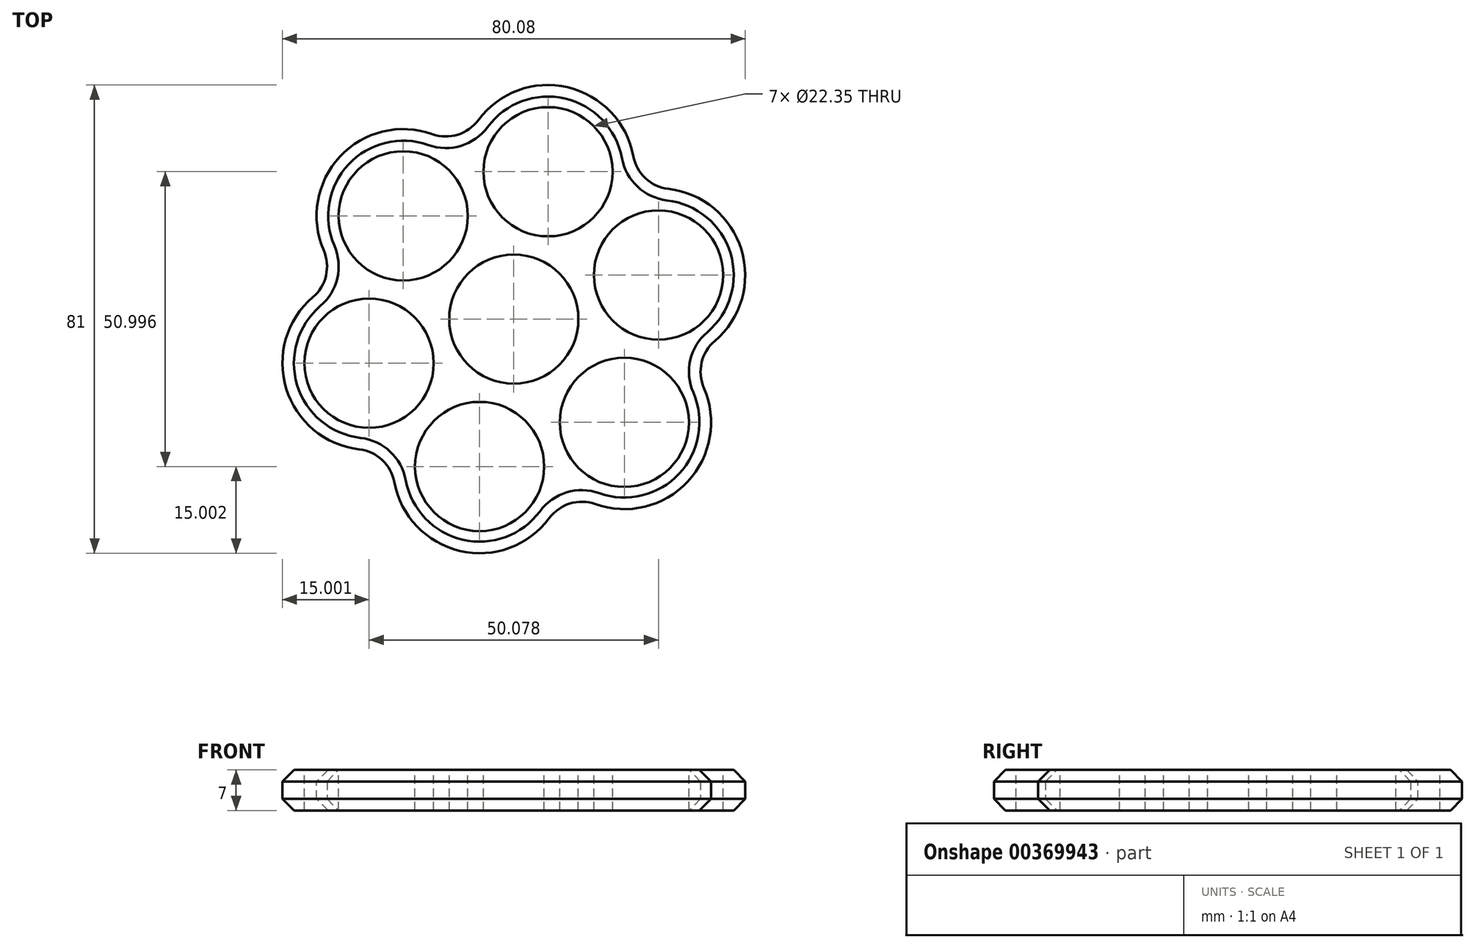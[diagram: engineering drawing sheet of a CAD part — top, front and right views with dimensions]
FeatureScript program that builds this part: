
annotation { "Feature Type Name" : "Feature", "Feature Type Description" : "" }
export const myFeature = defineFeature(function(context is Context, id is Id, definition is map)
    precondition{}
    {
        {
            var Q0;
            Q0=qCreatedBy(makeId("Top.planeOp"),FACE);
            var sketch = newSketch(context, id + "F0", { "sketchPlane" : qUnion([Q0])});
            skCircle(sketch, "E0", {"center": v(0, 0) * mm, "radius": 11.18 * mm});
            skLineSegment(sketch, "E1", {"start": v(0, 0) * mm, "end": v(-19.13, 17.87) * mm});
            skLineSegment(sketch, "E2", {"start": v(0, 0) * mm, "end": v(25.04, 7.63) * mm});
            skLineSegment(sketch, "E3", {"start": v(0, 0) * mm, "end": v(-5.91, -25.5) * mm});
            skCircle(sketch, "E4", {"center": v(-19.13, 17.87) * mm, "radius": 11.18 * mm});
            skCircle(sketch, "E5", {"center": v(25.04, 7.63) * mm, "radius": 11.18 * mm});
            skCircle(sketch, "E6", {"center": v(-5.91, -25.5) * mm, "radius": 11.18 * mm});
            skCircle(sketch, "E7", {"center": v(0, 0) * mm, "radius": 15 * mm});
            skCircle(sketch, "E8", {"center": v(-19.13, 17.87) * mm, "radius": 15 * mm});
            skCircle(sketch, "E9", {"center": v(25.04, 7.63) * mm, "radius": 15 * mm});
            skCircle(sketch, "E10", {"center": v(-5.91, -25.5) * mm, "radius": 15 * mm});
            skLineSegment(sketch, "E11", {"start": v(-19.13, 17.87) * mm, "end": v(-8.88, 28.83) * mm});
            skLineSegment(sketch, "E12", {"start": v(25.04, 7.63) * mm, "end": v(20.67, 21.98) * mm});
            skLineSegment(sketch, "E13", {"start": v(-5.91, -25.5) * mm, "end": v(8.7, -28.89) * mm});
            skLineSegment(sketch, "E14", {"start": v(-5.91, -25.5) * mm, "end": v(-20.53, -22.1) * mm});
            skLineSegment(sketch, "E15", {"start": v(-19.13, 17.87) * mm, "end": v(-29.37, 6.91) * mm});
            skLineSegment(sketch, "E16", {"start": v(25.04, 7.63) * mm, "end": v(29.41, -6.72) * mm});
            skLineSegment(sketch, "E17", {"start": v(0, 0) * mm, "end": v(5.91, 25.5) * mm});
            skLineSegment(sketch, "E18", {"start": v(0, 0) * mm, "end": v(19.13, -17.87) * mm});
            skLineSegment(sketch, "E19", {"start": v(0, 0) * mm, "end": v(-25.04, -7.63) * mm});
            skCircle(sketch, "E20", {"center": v(-25.04, -7.63) * mm, "radius": 11.18 * mm});
            skCircle(sketch, "E21", {"center": v(5.91, 25.5) * mm, "radius": 11.18 * mm});
            skCircle(sketch, "E22", {"center": v(19.13, -17.87) * mm, "radius": 11.18 * mm});
            skCircle(sketch, "E23", {"center": v(-25.04, -7.63) * mm, "radius": 15 * mm});
            skCircle(sketch, "E24", {"center": v(5.91, 25.5) * mm, "radius": 15 * mm});
            skCircle(sketch, "E25", {"center": v(19.13, -17.87) * mm, "radius": 15 * mm});
            skSolve(sketch);
        }
        {
            var Q0;
            {var subQ0=sQuery(id+"F0.wireOp",EDGE,"E11");var subQ1=sQuery(id+"F0.wireOp",EDGE,"E4");var subQ2=makeQuery(id+"F0.imprint","INTERSECT",VERTEX,{"derivedFrom":[subQ1,subQ0]});Q0=makeQuery(id+"F0.imprint","IMPRINT",FACE,{"disambiguationData":[TD([[makeQuery(id+"F0.imprint","IMPRINT",EDGE,{"disambiguationData":[TD([[subQ2,1.0]])],"derivedFrom":subQ1}),-1.0]])]});}
            var Q1;
            {var subQ0=sQuery(id+"F0.wireOp",EDGE,"E11");var subQ1=sQuery(id+"F0.wireOp",EDGE,"E4");var subQ2=makeQuery(id+"F0.imprint","INTERSECT",VERTEX,{"derivedFrom":[subQ1,subQ0]});Q1=makeQuery(id+"F0.imprint","IMPRINT",FACE,{"disambiguationData":[TD([[makeQuery(id+"F0.imprint","IMPRINT",EDGE,{"disambiguationData":[TD([[subQ2,-1.0]])],"derivedFrom":subQ1}),-1.0]])]});}
            var Q2;
            {var subQ0=sQuery(id+"F0.wireOp",EDGE,"E15");var subQ1=sQuery(id+"F0.wireOp",EDGE,"E4");var subQ2=makeQuery(id+"F0.imprint","INTERSECT",VERTEX,{"derivedFrom":[subQ1,subQ0]});Q2=makeQuery(id+"F0.imprint","IMPRINT",FACE,{"disambiguationData":[TD([[makeQuery(id+"F0.imprint","IMPRINT",EDGE,{"disambiguationData":[TD([[subQ2,-1.0]])],"derivedFrom":subQ1}),-1.0]])]});}
            var Q3;
            {var subQ0=sQuery(id+"F0.wireOp",EDGE,"E24");var subQ1=sQuery(id+"F0.wireOp",EDGE,"E5");var subQ2=makeQuery(id+"F0.imprint","INTERSECT",VERTEX,{"derivedFrom":[subQ1,subQ0]});Q3=makeQuery(id+"F0.imprint","IMPRINT",FACE,{"disambiguationData":[TD([[makeQuery(id+"F0.imprint","IMPRINT",EDGE,{"disambiguationData":[TD([[subQ2,1.0]])],"derivedFrom":subQ1}),-1.0]])]});}
            var Q4;
            {var subQ0=sQuery(id+"F0.wireOp",EDGE,"E25");var subQ1=sQuery(id+"F0.wireOp",EDGE,"E5");var subQ2=makeQuery(id+"F0.imprint","INTERSECT",VERTEX,{"derivedFrom":[subQ1,subQ0]});Q4=makeQuery(id+"F0.imprint","IMPRINT",FACE,{"disambiguationData":[TD([[makeQuery(id+"F0.imprint","IMPRINT",EDGE,{"disambiguationData":[TD([[subQ2,-1.0]])],"derivedFrom":subQ1}),-1.0]])]});}
            var Q5;
            {var subQ0=sQuery(id+"F0.wireOp",EDGE,"E12");var subQ1=sQuery(id+"F0.wireOp",EDGE,"E5");var subQ2=makeQuery(id+"F0.imprint","INTERSECT",VERTEX,{"derivedFrom":[subQ1,subQ0]});Q5=makeQuery(id+"F0.imprint","IMPRINT",FACE,{"disambiguationData":[TD([[makeQuery(id+"F0.imprint","IMPRINT",EDGE,{"disambiguationData":[TD([[subQ2,1.0]])],"derivedFrom":subQ1}),-1.0]])]});}
            var Q6;
            {var subQ0=sQuery(id+"F0.wireOp",EDGE,"E23");var subQ1=sQuery(id+"F0.wireOp",EDGE,"E6");var subQ2=makeQuery(id+"F0.imprint","INTERSECT",VERTEX,{"derivedFrom":[subQ1,subQ0]});Q6=makeQuery(id+"F0.imprint","IMPRINT",FACE,{"disambiguationData":[TD([[makeQuery(id+"F0.imprint","IMPRINT",EDGE,{"disambiguationData":[TD([[subQ2,-1.0]])],"derivedFrom":subQ1}),-1.0]])]});}
            var Q7;
            {var subQ0=sQuery(id+"F0.wireOp",EDGE,"E14");var subQ1=sQuery(id+"F0.wireOp",EDGE,"E6");var subQ2=makeQuery(id+"F0.imprint","INTERSECT",VERTEX,{"derivedFrom":[subQ1,subQ0]});Q7=makeQuery(id+"F0.imprint","IMPRINT",FACE,{"disambiguationData":[TD([[makeQuery(id+"F0.imprint","IMPRINT",EDGE,{"disambiguationData":[TD([[subQ2,-1.0]])],"derivedFrom":subQ1}),-1.0]])]});}
            var Q8;
            {var subQ0=sQuery(id+"F0.wireOp",EDGE,"E25");var subQ1=sQuery(id+"F0.wireOp",EDGE,"E6");var subQ2=makeQuery(id+"F0.imprint","INTERSECT",VERTEX,{"derivedFrom":[subQ1,subQ0]});Q8=makeQuery(id+"F0.imprint","IMPRINT",FACE,{"disambiguationData":[TD([[makeQuery(id+"F0.imprint","IMPRINT",EDGE,{"disambiguationData":[TD([[subQ2,1.0]])],"derivedFrom":subQ1}),-1.0]])]});}
            var Q9;
            {var subQ0=sQuery(id+"F0.wireOp",EDGE,"E24");var subQ1=sQuery(id+"F0.wireOp",EDGE,"E8");var subQ2=makeQuery(id+"F0.imprint","INTERSECT",VERTEX,{"disambiguationData":[OD(0.0)],"derivedFrom":[subQ1,subQ0]});Q9=makeQuery(id+"F0.imprint","IMPRINT",FACE,{"disambiguationData":[TD([[makeQuery(id+"F0.imprint","IMPRINT",EDGE,{"disambiguationData":[TD([[subQ2,1.0]])],"derivedFrom":subQ1}),-1.0]])]});}
            var Q10;
            {var subQ0=sQuery(id+"F0.wireOp",EDGE,"E23");var subQ1=sQuery(id+"F0.wireOp",EDGE,"E8");var subQ2=makeQuery(id+"F0.imprint","INTERSECT",VERTEX,{"disambiguationData":[OD(0.0)],"derivedFrom":[subQ1,subQ0]});Q10=makeQuery(id+"F0.imprint","IMPRINT",FACE,{"disambiguationData":[TD([[makeQuery(id+"F0.imprint","IMPRINT",EDGE,{"disambiguationData":[TD([[subQ2,-1.0]])],"derivedFrom":subQ1}),-1.0]])]});}
            var Q11;
            {var subQ0=sQuery(id+"F0.wireOp",EDGE,"E25");var subQ1=sQuery(id+"F0.wireOp",EDGE,"E9");var subQ2=makeQuery(id+"F0.imprint","INTERSECT",VERTEX,{"disambiguationData":[OD(0.0)],"derivedFrom":[subQ1,subQ0]});Q11=makeQuery(id+"F0.imprint","IMPRINT",FACE,{"disambiguationData":[TD([[makeQuery(id+"F0.imprint","IMPRINT",EDGE,{"disambiguationData":[TD([[subQ2,1.0]])],"derivedFrom":subQ1}),-1.0]])]});}
            var Q12;
            {var subQ0=sQuery(id+"F0.wireOp",EDGE,"E24");var subQ1=sQuery(id+"F0.wireOp",EDGE,"E8");var subQ2=makeQuery(id+"F0.imprint","INTERSECT",VERTEX,{"disambiguationData":[OD(0.0)],"derivedFrom":[subQ1,subQ0]});Q12=makeQuery(id+"F0.imprint","IMPRINT",FACE,{"disambiguationData":[TD([[makeQuery(id+"F0.imprint","IMPRINT",EDGE,{"disambiguationData":[TD([[subQ2,1.0]])],"derivedFrom":subQ1}),1.0]])]});}
            var Q13;
            {var subQ0=sQuery(id+"F0.wireOp",EDGE,"E23");var subQ1=sQuery(id+"F0.wireOp",EDGE,"E8");var subQ2=makeQuery(id+"F0.imprint","INTERSECT",VERTEX,{"disambiguationData":[OD(0.0)],"derivedFrom":[subQ1,subQ0]});Q13=makeQuery(id+"F0.imprint","IMPRINT",FACE,{"disambiguationData":[TD([[makeQuery(id+"F0.imprint","IMPRINT",EDGE,{"disambiguationData":[TD([[subQ2,-1.0]])],"derivedFrom":subQ1}),1.0]])]});}
            var Q14;
            {var subQ0=sQuery(id+"F0.wireOp",EDGE,"E24");var subQ1=sQuery(id+"F0.wireOp",EDGE,"E9");var subQ2=makeQuery(id+"F0.imprint","INTERSECT",VERTEX,{"disambiguationData":[OD(0.0)],"derivedFrom":[subQ1,subQ0]});Q14=makeQuery(id+"F0.imprint","IMPRINT",FACE,{"disambiguationData":[TD([[makeQuery(id+"F0.imprint","IMPRINT",EDGE,{"disambiguationData":[TD([[subQ2,-1.0]])],"derivedFrom":subQ1}),1.0]])]});}
            var Q15;
            {var subQ0=sQuery(id+"F0.wireOp",EDGE,"E25");var subQ1=sQuery(id+"F0.wireOp",EDGE,"E9");var subQ2=makeQuery(id+"F0.imprint","INTERSECT",VERTEX,{"disambiguationData":[OD(1.0)],"derivedFrom":[subQ1,subQ0]});Q15=makeQuery(id+"F0.imprint","IMPRINT",FACE,{"disambiguationData":[TD([[makeQuery(id+"F0.imprint","IMPRINT",EDGE,{"disambiguationData":[TD([[subQ2,-1.0]])],"derivedFrom":subQ1}),1.0]])]});}
            var Q16;
            {var subQ0=sQuery(id+"F0.wireOp",EDGE,"E25");var subQ1=sQuery(id+"F0.wireOp",EDGE,"E10");var subQ2=makeQuery(id+"F0.imprint","INTERSECT",VERTEX,{"disambiguationData":[OD(1.0)],"derivedFrom":[subQ1,subQ0]});Q16=makeQuery(id+"F0.imprint","IMPRINT",FACE,{"disambiguationData":[TD([[makeQuery(id+"F0.imprint","IMPRINT",EDGE,{"disambiguationData":[TD([[subQ2,1.0]])],"derivedFrom":subQ1}),1.0]])]});}
            var Q17;
            {var subQ0=sQuery(id+"F0.wireOp",EDGE,"E23");var subQ1=sQuery(id+"F0.wireOp",EDGE,"E10");var subQ2=makeQuery(id+"F0.imprint","INTERSECT",VERTEX,{"disambiguationData":[OD(1.0)],"derivedFrom":[subQ1,subQ0]});Q17=makeQuery(id+"F0.imprint","IMPRINT",FACE,{"disambiguationData":[TD([[makeQuery(id+"F0.imprint","IMPRINT",EDGE,{"disambiguationData":[TD([[subQ2,-1.0]])],"derivedFrom":subQ1}),1.0]])]});}
            var Q18;
            {var subQ3=sQuery(id+"F0.wireOp",EDGE,"E7");var subQ5=sQuery(id+"F0.wireOp",EDGE,"E8");var subQ6=makeQuery(id+"F0.imprint","INTERSECT",VERTEX,{"disambiguationData":[OD(0.0)],"derivedFrom":[subQ3,subQ5]});Q18=makeQuery(id+"F0.imprint","IMPRINT",FACE,{"disambiguationData":[TD([[makeQuery(id+"F0.imprint","IMPRINT",EDGE,{"disambiguationData":[TD([[subQ6,-1.0]])],"derivedFrom":subQ5}),1.0]])]});}
            var Q19;
            {var subQ0=sQuery(id+"F0.wireOp",EDGE,"E8");var subQ3=sQuery(id+"F0.wireOp",EDGE,"E7");var subQ5=makeQuery(id+"F0.imprint","INTERSECT",VERTEX,{"disambiguationData":[OD(1.0)],"derivedFrom":[subQ3,subQ0]});Q19=makeQuery(id+"F0.imprint","IMPRINT",FACE,{"disambiguationData":[TD([[makeQuery(id+"F0.imprint","IMPRINT",EDGE,{"disambiguationData":[TD([[subQ5,1.0]])],"derivedFrom":subQ3}),1.0]])]});}
            var Q20;
            {var subQ3=sQuery(id+"F0.wireOp",EDGE,"E7");var subQ5=sQuery(id+"F0.wireOp",EDGE,"E8");var subQ6=makeQuery(id+"F0.imprint","INTERSECT",VERTEX,{"disambiguationData":[OD(1.0)],"derivedFrom":[subQ3,subQ5]});Q20=makeQuery(id+"F0.imprint","IMPRINT",FACE,{"disambiguationData":[TD([[makeQuery(id+"F0.imprint","IMPRINT",EDGE,{"disambiguationData":[TD([[subQ6,1.0]])],"derivedFrom":subQ5}),1.0]])]});}
            var Q21;
            {var subQ0=sQuery(id+"F0.wireOp",EDGE,"E8");var subQ3=sQuery(id+"F0.wireOp",EDGE,"E7");var subQ5=makeQuery(id+"F0.imprint","INTERSECT",VERTEX,{"disambiguationData":[OD(0.0)],"derivedFrom":[subQ3,subQ0]});Q21=makeQuery(id+"F0.imprint","IMPRINT",FACE,{"disambiguationData":[TD([[makeQuery(id+"F0.imprint","IMPRINT",EDGE,{"disambiguationData":[TD([[subQ5,-1.0]])],"derivedFrom":subQ3}),1.0]])]});}
            var Q22;
            {var subQ3=sQuery(id+"F0.wireOp",EDGE,"E21");var subQ5=sQuery(id+"F0.wireOp",EDGE,"E8");var subQ6=makeQuery(id+"F0.imprint","INTERSECT",VERTEX,{"derivedFrom":[subQ5,subQ3]});Q22=makeQuery(id+"F0.imprint","IMPRINT",FACE,{"disambiguationData":[TD([[makeQuery(id+"F0.imprint","IMPRINT",EDGE,{"disambiguationData":[TD([[subQ6,1.0]])],"derivedFrom":subQ5}),-1.0]])]});}
            var Q23;
            {var subQ0=sQuery(id+"F0.wireOp",EDGE,"E24");var subQ1=sQuery(id+"F0.wireOp",EDGE,"E7");var subQ2=makeQuery(id+"F0.imprint","INTERSECT",VERTEX,{"disambiguationData":[OD(1.0)],"derivedFrom":[subQ1,subQ0]});Q23=makeQuery(id+"F0.imprint","IMPRINT",FACE,{"disambiguationData":[TD([[makeQuery(id+"F0.imprint","IMPRINT",EDGE,{"disambiguationData":[TD([[subQ2,1.0]])],"derivedFrom":subQ1}),1.0]])]});}
            var Q24;
            {var subQ0=sQuery(id+"F0.wireOp",EDGE,"E24");var subQ1=sQuery(id+"F0.wireOp",EDGE,"E7");var subQ2=makeQuery(id+"F0.imprint","INTERSECT",VERTEX,{"disambiguationData":[OD(0.0)],"derivedFrom":[subQ1,subQ0]});Q24=makeQuery(id+"F0.imprint","IMPRINT",FACE,{"disambiguationData":[TD([[makeQuery(id+"F0.imprint","IMPRINT",EDGE,{"disambiguationData":[TD([[subQ2,-1.0]])],"derivedFrom":subQ1}),1.0]])]});}
            var Q25;
            {var subQ3=sQuery(id+"F0.wireOp",EDGE,"E21");var subQ5=sQuery(id+"F0.wireOp",EDGE,"E9");var subQ7=makeQuery(id+"F0.imprint","INTERSECT",VERTEX,{"derivedFrom":[subQ5,subQ3]});Q25=makeQuery(id+"F0.imprint","IMPRINT",FACE,{"disambiguationData":[TD([[makeQuery(id+"F0.imprint","IMPRINT",EDGE,{"disambiguationData":[TD([[subQ7,-1.0]])],"derivedFrom":subQ5}),-1.0]])]});}
            var Q26;
            {var subQ3=sQuery(id+"F0.wireOp",EDGE,"E7");var subQ5=sQuery(id+"F0.wireOp",EDGE,"E9");var subQ6=makeQuery(id+"F0.imprint","INTERSECT",VERTEX,{"disambiguationData":[OD(0.0)],"derivedFrom":[subQ3,subQ5]});Q26=makeQuery(id+"F0.imprint","IMPRINT",FACE,{"disambiguationData":[TD([[makeQuery(id+"F0.imprint","IMPRINT",EDGE,{"disambiguationData":[TD([[subQ6,1.0]])],"derivedFrom":subQ5}),1.0]])]});}
            var Q27;
            {var subQ0=sQuery(id+"F0.wireOp",EDGE,"E9");var subQ3=sQuery(id+"F0.wireOp",EDGE,"E7");var subQ5=makeQuery(id+"F0.imprint","INTERSECT",VERTEX,{"disambiguationData":[OD(0.0)],"derivedFrom":[subQ3,subQ0]});Q27=makeQuery(id+"F0.imprint","IMPRINT",FACE,{"disambiguationData":[TD([[makeQuery(id+"F0.imprint","IMPRINT",EDGE,{"disambiguationData":[TD([[subQ5,1.0]])],"derivedFrom":subQ3}),1.0]])]});}
            var Q28;
            {var subQ0=sQuery(id+"F0.wireOp",EDGE,"E9");var subQ3=sQuery(id+"F0.wireOp",EDGE,"E7");var subQ5=makeQuery(id+"F0.imprint","INTERSECT",VERTEX,{"disambiguationData":[OD(1.0)],"derivedFrom":[subQ3,subQ0]});Q28=makeQuery(id+"F0.imprint","IMPRINT",FACE,{"disambiguationData":[TD([[makeQuery(id+"F0.imprint","IMPRINT",EDGE,{"disambiguationData":[TD([[subQ5,-1.0]])],"derivedFrom":subQ3}),1.0]])]});}
            var Q29;
            {var subQ3=sQuery(id+"F0.wireOp",EDGE,"E7");var subQ5=sQuery(id+"F0.wireOp",EDGE,"E9");var subQ6=makeQuery(id+"F0.imprint","INTERSECT",VERTEX,{"disambiguationData":[OD(1.0)],"derivedFrom":[subQ3,subQ5]});Q29=makeQuery(id+"F0.imprint","IMPRINT",FACE,{"disambiguationData":[TD([[makeQuery(id+"F0.imprint","IMPRINT",EDGE,{"disambiguationData":[TD([[subQ6,-1.0]])],"derivedFrom":subQ5}),1.0]])]});}
            var Q30;
            {var subQ0=sQuery(id+"F0.wireOp",EDGE,"E8");var subQ5=sQuery(id+"F0.wireOp",EDGE,"E7");var subQ6=makeQuery(id+"F0.imprint","INTERSECT",VERTEX,{"disambiguationData":[OD(1.0)],"derivedFrom":[subQ5,subQ0]});Q30=makeQuery(id+"F0.imprint","IMPRINT",FACE,{"disambiguationData":[TD([[makeQuery(id+"F0.imprint","IMPRINT",EDGE,{"disambiguationData":[TD([[subQ6,-1.0]])],"derivedFrom":subQ5}),1.0]])]});}
            var Q31;
            {var subQ3=sQuery(id+"F0.wireOp",EDGE,"E20");var subQ5=sQuery(id+"F0.wireOp",EDGE,"E8");var subQ6=makeQuery(id+"F0.imprint","INTERSECT",VERTEX,{"derivedFrom":[subQ5,subQ3]});Q31=makeQuery(id+"F0.imprint","IMPRINT",FACE,{"disambiguationData":[TD([[makeQuery(id+"F0.imprint","IMPRINT",EDGE,{"disambiguationData":[TD([[subQ6,-1.0]])],"derivedFrom":subQ5}),-1.0]])]});}
            var Q32;
            {var subQ0=sQuery(id+"F0.wireOp",EDGE,"E23");var subQ1=sQuery(id+"F0.wireOp",EDGE,"E7");var subQ2=makeQuery(id+"F0.imprint","INTERSECT",VERTEX,{"disambiguationData":[OD(0.0)],"derivedFrom":[subQ1,subQ0]});Q32=makeQuery(id+"F0.imprint","IMPRINT",FACE,{"disambiguationData":[TD([[makeQuery(id+"F0.imprint","IMPRINT",EDGE,{"disambiguationData":[TD([[subQ2,-1.0]])],"derivedFrom":subQ1}),1.0]])]});}
            var Q33;
            {var subQ0=sQuery(id+"F0.wireOp",EDGE,"E23");var subQ1=sQuery(id+"F0.wireOp",EDGE,"E7");var subQ2=makeQuery(id+"F0.imprint","INTERSECT",VERTEX,{"disambiguationData":[OD(1.0)],"derivedFrom":[subQ1,subQ0]});Q33=makeQuery(id+"F0.imprint","IMPRINT",FACE,{"disambiguationData":[TD([[makeQuery(id+"F0.imprint","IMPRINT",EDGE,{"disambiguationData":[TD([[subQ2,1.0]])],"derivedFrom":subQ1}),1.0]])]});}
            var Q34;
            {var subQ0=sQuery(id+"F0.wireOp",EDGE,"E23");var subQ5=sQuery(id+"F0.wireOp",EDGE,"E10");var subQ6=makeQuery(id+"F0.imprint","INTERSECT",VERTEX,{"disambiguationData":[OD(1.0)],"derivedFrom":[subQ5,subQ0]});Q34=makeQuery(id+"F0.imprint","IMPRINT",FACE,{"disambiguationData":[TD([[makeQuery(id+"F0.imprint","IMPRINT",EDGE,{"disambiguationData":[TD([[subQ6,-1.0]])],"derivedFrom":subQ5}),-1.0]])]});}
            var Q35;
            {var subQ0=sQuery(id+"F0.wireOp",EDGE,"E23");var subQ5=sQuery(id+"F0.wireOp",EDGE,"E7");var subQ7=makeQuery(id+"F0.imprint","INTERSECT",VERTEX,{"disambiguationData":[OD(1.0)],"derivedFrom":[subQ5,subQ0]});Q35=makeQuery(id+"F0.imprint","IMPRINT",FACE,{"disambiguationData":[TD([[makeQuery(id+"F0.imprint","IMPRINT",EDGE,{"disambiguationData":[TD([[subQ7,-1.0]])],"derivedFrom":subQ5}),1.0]])]});}
            var Q36;
            {var subQ0=sQuery(id+"F0.wireOp",EDGE,"E10");var subQ3=sQuery(id+"F0.wireOp",EDGE,"E7");var subQ5=makeQuery(id+"F0.imprint","INTERSECT",VERTEX,{"disambiguationData":[OD(0.0)],"derivedFrom":[subQ3,subQ0]});Q36=makeQuery(id+"F0.imprint","IMPRINT",FACE,{"disambiguationData":[TD([[makeQuery(id+"F0.imprint","IMPRINT",EDGE,{"disambiguationData":[TD([[subQ5,-1.0]])],"derivedFrom":subQ3}),1.0]])]});}
            var Q37;
            {var subQ3=sQuery(id+"F0.wireOp",EDGE,"E7");var subQ5=sQuery(id+"F0.wireOp",EDGE,"E10");var subQ6=makeQuery(id+"F0.imprint","INTERSECT",VERTEX,{"disambiguationData":[OD(0.0)],"derivedFrom":[subQ3,subQ5]});Q37=makeQuery(id+"F0.imprint","IMPRINT",FACE,{"disambiguationData":[TD([[makeQuery(id+"F0.imprint","IMPRINT",EDGE,{"disambiguationData":[TD([[subQ6,-1.0]])],"derivedFrom":subQ5}),1.0]])]});}
            var Q38;
            {var subQ0=sQuery(id+"F0.wireOp",EDGE,"E10");var subQ3=sQuery(id+"F0.wireOp",EDGE,"E7");var subQ5=makeQuery(id+"F0.imprint","INTERSECT",VERTEX,{"disambiguationData":[OD(1.0)],"derivedFrom":[subQ3,subQ0]});Q38=makeQuery(id+"F0.imprint","IMPRINT",FACE,{"disambiguationData":[TD([[makeQuery(id+"F0.imprint","IMPRINT",EDGE,{"disambiguationData":[TD([[subQ5,1.0]])],"derivedFrom":subQ3}),1.0]])]});}
            var Q39;
            {var subQ3=sQuery(id+"F0.wireOp",EDGE,"E7");var subQ5=sQuery(id+"F0.wireOp",EDGE,"E10");var subQ6=makeQuery(id+"F0.imprint","INTERSECT",VERTEX,{"disambiguationData":[OD(1.0)],"derivedFrom":[subQ3,subQ5]});Q39=makeQuery(id+"F0.imprint","IMPRINT",FACE,{"disambiguationData":[TD([[makeQuery(id+"F0.imprint","IMPRINT",EDGE,{"disambiguationData":[TD([[subQ6,1.0]])],"derivedFrom":subQ5}),1.0]])]});}
            var Q40;
            {var subQ0=sQuery(id+"F0.wireOp",EDGE,"E10");var subQ5=sQuery(id+"F0.wireOp",EDGE,"E7");var subQ6=makeQuery(id+"F0.imprint","INTERSECT",VERTEX,{"disambiguationData":[OD(1.0)],"derivedFrom":[subQ5,subQ0]});Q40=makeQuery(id+"F0.imprint","IMPRINT",FACE,{"disambiguationData":[TD([[makeQuery(id+"F0.imprint","IMPRINT",EDGE,{"disambiguationData":[TD([[subQ6,-1.0]])],"derivedFrom":subQ5}),1.0]])]});}
            var Q41;
            {var subQ3=sQuery(id+"F0.wireOp",EDGE,"E25");var subQ5=sQuery(id+"F0.wireOp",EDGE,"E7");var subQ6=makeQuery(id+"F0.imprint","INTERSECT",VERTEX,{"disambiguationData":[OD(1.0)],"derivedFrom":[subQ5,subQ3]});Q41=makeQuery(id+"F0.imprint","IMPRINT",FACE,{"disambiguationData":[TD([[makeQuery(id+"F0.imprint","IMPRINT",EDGE,{"disambiguationData":[TD([[subQ6,-1.0]])],"derivedFrom":subQ5}),1.0]])]});}
            var Q42;
            {var subQ0=sQuery(id+"F0.wireOp",EDGE,"E25");var subQ5=sQuery(id+"F0.wireOp",EDGE,"E9");var subQ7=makeQuery(id+"F0.imprint","INTERSECT",VERTEX,{"disambiguationData":[OD(1.0)],"derivedFrom":[subQ5,subQ0]});Q42=makeQuery(id+"F0.imprint","IMPRINT",FACE,{"disambiguationData":[TD([[makeQuery(id+"F0.imprint","IMPRINT",EDGE,{"disambiguationData":[TD([[subQ7,-1.0]])],"derivedFrom":subQ5}),-1.0]])]});}
            var Q43;
            {var subQ0=sQuery(id+"F0.wireOp",EDGE,"E25");var subQ1=sQuery(id+"F0.wireOp",EDGE,"E7");var subQ2=makeQuery(id+"F0.imprint","INTERSECT",VERTEX,{"disambiguationData":[OD(1.0)],"derivedFrom":[subQ1,subQ0]});Q43=makeQuery(id+"F0.imprint","IMPRINT",FACE,{"disambiguationData":[TD([[makeQuery(id+"F0.imprint","IMPRINT",EDGE,{"disambiguationData":[TD([[subQ2,1.0]])],"derivedFrom":subQ1}),1.0]])]});}
            var Q44;
            {var subQ0=sQuery(id+"F0.wireOp",EDGE,"E25");var subQ1=sQuery(id+"F0.wireOp",EDGE,"E7");var subQ2=makeQuery(id+"F0.imprint","INTERSECT",VERTEX,{"disambiguationData":[OD(0.0)],"derivedFrom":[subQ1,subQ0]});Q44=makeQuery(id+"F0.imprint","IMPRINT",FACE,{"disambiguationData":[TD([[makeQuery(id+"F0.imprint","IMPRINT",EDGE,{"disambiguationData":[TD([[subQ2,-1.0]])],"derivedFrom":subQ1}),1.0]])]});}
            var Q45;
            {var subQ0=sQuery(id+"F0.wireOp",EDGE,"E25");var subQ5=sQuery(id+"F0.wireOp",EDGE,"E10");var subQ6=makeQuery(id+"F0.imprint","INTERSECT",VERTEX,{"disambiguationData":[OD(1.0)],"derivedFrom":[subQ5,subQ0]});Q45=makeQuery(id+"F0.imprint","IMPRINT",FACE,{"disambiguationData":[TD([[makeQuery(id+"F0.imprint","IMPRINT",EDGE,{"disambiguationData":[TD([[subQ6,1.0]])],"derivedFrom":subQ5}),-1.0]])]});}
            var Q46;
            {var subQ0=sQuery(id+"F0.wireOp",EDGE,"E24");var subQ5=sQuery(id+"F0.wireOp",EDGE,"E7");var subQ7=makeQuery(id+"F0.imprint","INTERSECT",VERTEX,{"disambiguationData":[OD(1.0)],"derivedFrom":[subQ5,subQ0]});Q46=makeQuery(id+"F0.imprint","IMPRINT",FACE,{"disambiguationData":[TD([[makeQuery(id+"F0.imprint","IMPRINT",EDGE,{"disambiguationData":[TD([[subQ7,-1.0]])],"derivedFrom":subQ5}),1.0]])]});}
            var Q47;
            {var subQ3=sQuery(id+"F0.wireOp",EDGE,"E9");var subQ5=sQuery(id+"F0.wireOp",EDGE,"E7");var subQ6=makeQuery(id+"F0.imprint","INTERSECT",VERTEX,{"disambiguationData":[OD(0.0)],"derivedFrom":[subQ5,subQ3]});Q47=makeQuery(id+"F0.imprint","IMPRINT",FACE,{"disambiguationData":[TD([[makeQuery(id+"F0.imprint","IMPRINT",EDGE,{"disambiguationData":[TD([[subQ6,-1.0]])],"derivedFrom":subQ5}),1.0]])]});}
            var Q48;
            {var subQ0=sQuery(id+"F0.wireOp",EDGE,"E10");var subQ1=sQuery(id+"F0.wireOp",EDGE,"E7");var subQ2=makeQuery(id+"F0.imprint","INTERSECT",VERTEX,{"disambiguationData":[OD(1.0)],"derivedFrom":[subQ1,subQ0]});Q48=makeQuery(id+"F0.imprint","IMPRINT",FACE,{"disambiguationData":[TD([[makeQuery(id+"F0.imprint","IMPRINT",EDGE,{"disambiguationData":[TD([[subQ2,-1.0]])],"derivedFrom":subQ1}),-1.0]])]});}
            var Q49;
            {var subQ0=sQuery(id+"F0.wireOp",EDGE,"E23");var subQ1=sQuery(id+"F0.wireOp",EDGE,"E7");var subQ2=makeQuery(id+"F0.imprint","INTERSECT",VERTEX,{"disambiguationData":[OD(1.0)],"derivedFrom":[subQ1,subQ0]});Q49=makeQuery(id+"F0.imprint","IMPRINT",FACE,{"disambiguationData":[TD([[makeQuery(id+"F0.imprint","IMPRINT",EDGE,{"disambiguationData":[TD([[subQ2,-1.0]])],"derivedFrom":subQ1}),-1.0]])]});}
            var Q50;
            {var subQ0=sQuery(id+"F0.wireOp",EDGE,"E8");var subQ1=sQuery(id+"F0.wireOp",EDGE,"E7");var subQ2=makeQuery(id+"F0.imprint","INTERSECT",VERTEX,{"disambiguationData":[OD(1.0)],"derivedFrom":[subQ1,subQ0]});Q50=makeQuery(id+"F0.imprint","IMPRINT",FACE,{"disambiguationData":[TD([[makeQuery(id+"F0.imprint","IMPRINT",EDGE,{"disambiguationData":[TD([[subQ2,-1.0]])],"derivedFrom":subQ1}),-1.0]])]});}
            var Q51;
            {var subQ0=sQuery(id+"F0.wireOp",EDGE,"E24");var subQ1=sQuery(id+"F0.wireOp",EDGE,"E7");var subQ2=makeQuery(id+"F0.imprint","INTERSECT",VERTEX,{"disambiguationData":[OD(1.0)],"derivedFrom":[subQ1,subQ0]});Q51=makeQuery(id+"F0.imprint","IMPRINT",FACE,{"disambiguationData":[TD([[makeQuery(id+"F0.imprint","IMPRINT",EDGE,{"disambiguationData":[TD([[subQ2,-1.0]])],"derivedFrom":subQ1}),-1.0]])]});}
            var Q52;
            {var subQ0=sQuery(id+"F0.wireOp",EDGE,"E9");var subQ1=sQuery(id+"F0.wireOp",EDGE,"E7");var subQ2=makeQuery(id+"F0.imprint","INTERSECT",VERTEX,{"disambiguationData":[OD(0.0)],"derivedFrom":[subQ1,subQ0]});Q52=makeQuery(id+"F0.imprint","IMPRINT",FACE,{"disambiguationData":[TD([[makeQuery(id+"F0.imprint","IMPRINT",EDGE,{"disambiguationData":[TD([[subQ2,-1.0]])],"derivedFrom":subQ1}),-1.0]])]});}
            var Q53;
            {var subQ0=sQuery(id+"F0.wireOp",EDGE,"E25");var subQ1=sQuery(id+"F0.wireOp",EDGE,"E7");var subQ2=makeQuery(id+"F0.imprint","INTERSECT",VERTEX,{"disambiguationData":[OD(1.0)],"derivedFrom":[subQ1,subQ0]});Q53=makeQuery(id+"F0.imprint","IMPRINT",FACE,{"disambiguationData":[TD([[makeQuery(id+"F0.imprint","IMPRINT",EDGE,{"disambiguationData":[TD([[subQ2,-1.0]])],"derivedFrom":subQ1}),-1.0]])]});}
            extrude(context, id + "F1", {"entities" : qUnion([Q0, Q1, Q2, Q3, Q4, Q5, Q6, Q7, Q8, Q9, Q10, Q11, Q12, Q13, Q14, Q15, Q16, Q17, Q18, Q19, Q20, Q21, Q22, Q23, Q24, Q25, Q26, Q27, Q28, Q29, Q30, Q31, Q32, Q33, Q34, Q35, Q36, Q37, Q38, Q39, Q40, Q41, Q42, Q43, Q44, Q45, Q46, Q47, Q48, Q49, Q50, Q51, Q52, Q53]), "oppositeDirection" : true, "depth" : 7 * mm, "offsetDistance" : 25 * mm});
        }
        {
            var Q0;
            {var subQ0=sQuery(id+"F0.wireOp",EDGE,"E23");var subQ1=sQuery(id+"F0.wireOp",EDGE,"E10");Q0=makeQuery(id+"F1.opExtrude","SWEPT_EDGE",EDGE,{"disambiguationData":[OSD([subQ1,subQ0]),TDD([makeQuery(id+"F0.imprint","INTERSECT",VERTEX,{"disambiguationData":[OD(0.0)],"derivedFrom":[subQ1,subQ0]})])]});}
            var Q1;
            {var subQ0=sQuery(id+"F0.wireOp",EDGE,"E25");var subQ1=sQuery(id+"F0.wireOp",EDGE,"E10");Q1=makeQuery(id+"F1.opExtrude","SWEPT_EDGE",EDGE,{"disambiguationData":[OSD([subQ1,subQ0]),TDD([makeQuery(id+"F0.imprint","INTERSECT",VERTEX,{"disambiguationData":[OD(0.0)],"derivedFrom":[subQ1,subQ0]})])]});}
            var Q2;
            {var subQ0=sQuery(id+"F0.wireOp",EDGE,"E25");var subQ1=sQuery(id+"F0.wireOp",EDGE,"E9");Q2=makeQuery(id+"F1.opExtrude","SWEPT_EDGE",EDGE,{"disambiguationData":[OSD([subQ1,subQ0]),TDD([makeQuery(id+"F0.imprint","INTERSECT",VERTEX,{"disambiguationData":[OD(0.0)],"derivedFrom":[subQ1,subQ0]})])]});}
            var Q3;
            {var subQ0=sQuery(id+"F0.wireOp",EDGE,"E24");var subQ1=sQuery(id+"F0.wireOp",EDGE,"E9");Q3=makeQuery(id+"F1.opExtrude","SWEPT_EDGE",EDGE,{"disambiguationData":[OSD([subQ1,subQ0]),TDD([makeQuery(id+"F0.imprint","INTERSECT",VERTEX,{"disambiguationData":[OD(0.0)],"derivedFrom":[subQ1,subQ0]})])]});}
            var Q4;
            {var subQ0=sQuery(id+"F0.wireOp",EDGE,"E24");var subQ1=sQuery(id+"F0.wireOp",EDGE,"E8");Q4=makeQuery(id+"F1.opExtrude","SWEPT_EDGE",EDGE,{"disambiguationData":[OSD([subQ1,subQ0]),TDD([makeQuery(id+"F0.imprint","INTERSECT",VERTEX,{"disambiguationData":[OD(0.0)],"derivedFrom":[subQ1,subQ0]})])]});}
            var Q5;
            {var subQ0=sQuery(id+"F0.wireOp",EDGE,"E23");var subQ1=sQuery(id+"F0.wireOp",EDGE,"E8");Q5=makeQuery(id+"F1.opExtrude","SWEPT_EDGE",EDGE,{"disambiguationData":[OSD([subQ1,subQ0]),TDD([makeQuery(id+"F0.imprint","INTERSECT",VERTEX,{"disambiguationData":[OD(0.0)],"derivedFrom":[subQ1,subQ0]})])]});}
            fillet(context, id + "F2", {"entities" : qUnion([Q0, Q1, Q2, Q3, Q4, Q5]), "radius" : 7 * mm, "tangentPropagation" : true, "allowEdgeOverflow" : false});
        }
        {
            var Q0;
            {var subQ0=sQuery(id+"F0.wireOp",EDGE,"E25");Q0=makeQuery(id+"F1.opExtrude","CAP_EDGE",EDGE,{"disambiguationData":[OSD([subQ0]),TDD([makeQuery(id+"F0.imprint","IMPRINT",EDGE,{"disambiguationData":[TD([[makeQuery(id+"F0.imprint","INTERSECT",VERTEX,{"disambiguationData":[OD(0.0)],"derivedFrom":[sQuery(id+"F0.wireOp",EDGE,"E9"),subQ0]}),1.0]])],"derivedFrom":subQ0})])],"isStart":true});}
            var Q1;
            {var subQ0=sQuery(id+"F0.wireOp",EDGE,"E25");Q1=makeQuery(id+"F1.opExtrude","CAP_EDGE",EDGE,{"disambiguationData":[OSD([subQ0]),TDD([makeQuery(id+"F0.imprint","IMPRINT",EDGE,{"disambiguationData":[TD([[makeQuery(id+"F0.imprint","INTERSECT",VERTEX,{"disambiguationData":[OD(0.0)],"derivedFrom":[sQuery(id+"F0.wireOp",EDGE,"E9"),subQ0]}),1.0]])],"derivedFrom":subQ0})])],"isStart":false});}
            chamfer(context, id + "F3", {"entities" : qUnion([Q0, Q1]), "width" : 2 * mm, "tangentPropagation" : true});
        }
    });
